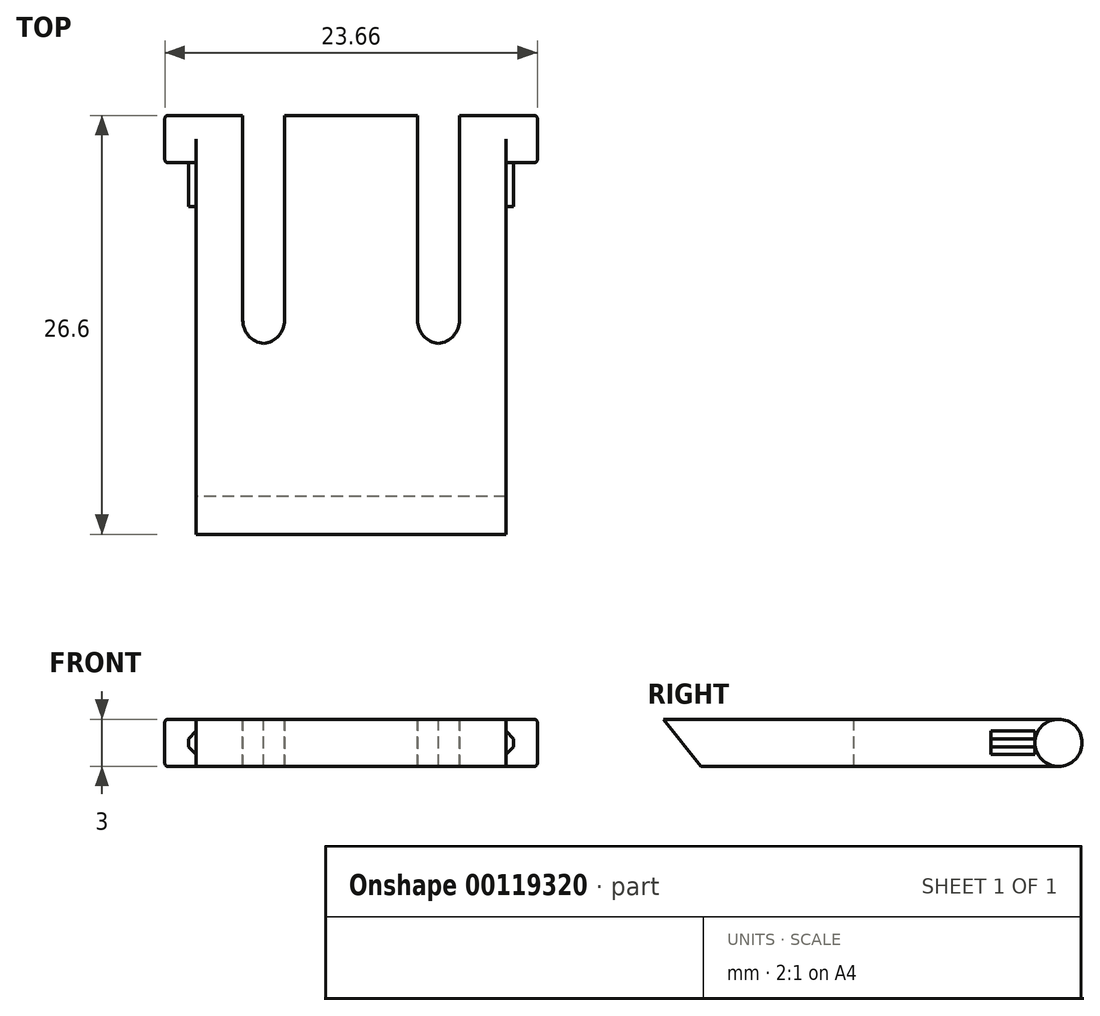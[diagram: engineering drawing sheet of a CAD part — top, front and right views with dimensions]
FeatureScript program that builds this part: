
annotation { "Feature Type Name" : "Feature", "Feature Type Description" : "" }
export const myFeature = defineFeature(function(context is Context, id is Id, definition is map)
    precondition{}
    {
        {
            var Q0;
            Q0=qCreatedBy(makeId("Top.planeOp"),FACE);
            var sketch = newSketch(context, id + "F0", { "sketchPlane" : qUnion([Q0])});
            skLineSegment(sketch, "E0.bottom", {"start": v(-29.8, 15.65) * mm, "end": v(-10.13, 15.65) * mm});
            skLineSegment(sketch, "E0.top", {"start": v(-29.8, -10.95) * mm, "end": v(-10.13, -10.95) * mm});
            skLineSegment(sketch, "E0.left", {"start": v(-29.8, 15.65) * mm, "end": v(-29.8, -10.95) * mm});
            skLineSegment(sketch, "E0.right", {"start": v(-10.13, 15.65) * mm, "end": v(-10.13, -10.95) * mm});
            skPoint(sketch, "E1", {"position": v(-13.08, 15.65) * mm});
            skPoint(sketch, "E2", {"position": v(-26.84, 15.65) * mm});
            skPoint(sketch, "E3", {"position": v(-24.18, 15.65) * mm});
            skPoint(sketch, "E4", {"position": v(-15.74, 15.65) * mm});
            skLineSegment(sketch, "E5.bottom", {"start": v(-26.84, 15.65) * mm, "end": v(-24.18, 15.65) * mm});
            skLineSegment(sketch, "E5.top", {"start": v(-26.84, 1.15) * mm, "end": v(-24.18, 1.15) * mm});
            skLineSegment(sketch, "E5.left", {"start": v(-26.84, 15.65) * mm, "end": v(-26.84, 1.15) * mm});
            skLineSegment(sketch, "E5.right", {"start": v(-24.18, 15.65) * mm, "end": v(-24.18, 1.15) * mm});
            skLineSegment(sketch, "E6.bottom", {"start": v(-13.08, 15.65) * mm, "end": v(-15.74, 15.65) * mm});
            skLineSegment(sketch, "E6.top", {"start": v(-13.08, 1.15) * mm, "end": v(-15.74, 1.15) * mm});
            skLineSegment(sketch, "E6.left", {"start": v(-13.08, 15.65) * mm, "end": v(-13.08, 1.15) * mm});
            skLineSegment(sketch, "E6.right", {"start": v(-15.74, 15.65) * mm, "end": v(-15.74, 1.15) * mm});
            skSolve(sketch);
        }
        {
            var Q0;
            Q0=makeQuery(id+"F0.imprint","IMPRINT",FACE,{"disambiguationData":[TD([[makeQuery(id+"F0.imprint","IMPRINT",EDGE,{"derivedFrom":sQuery(id+"F0.wireOp",EDGE,"E0.top")}),1.0]])]});
            extrude(context, id + "F1", {"entities" : qUnion([Q0]), "depth" : 3 * mm});
        }
        {
            var Q0;
            Q0=makeQuery(id+"F1.opExtrude","SWEPT_FACE",FACE,{"disambiguationData":[OSD([sQuery(id+"F0.wireOp",EDGE,"E0.right")])]});
            var sketch = newSketch(context, id + "F2", { "sketchPlane" : qUnion([Q0])});
            skPoint(sketch, "E7", {"position": v(14.15, 1.5) * mm});
            skPoint(sketch, "E7.positionSnap0", {"position": v(15.65, 1.5) * mm});
            skCircle(sketch, "E8", {"center": v(14.15, 1.5) * mm, "radius": 1.5 * mm});
            skPoint(sketch, "E9", {"position": v(12.65, 1.5) * mm});
            skPoint(sketch, "E10", {"position": v(12.65, 2.25) * mm});
            skLineSegment(sketch, "E11.bottom", {"start": v(12.65, 2.25) * mm, "end": v(9.85, 2.25) * mm});
            skLineSegment(sketch, "E11.top", {"start": v(12.65, 0.75) * mm, "end": v(9.85, 0.75) * mm});
            skLineSegment(sketch, "E11.left", {"start": v(12.65, 2.25) * mm, "end": v(12.65, 0.75) * mm});
            skLineSegment(sketch, "E11.right", {"start": v(9.85, 2.25) * mm, "end": v(9.85, 0.75) * mm});
            skSolve(sketch);
        }
        {
            var Q0;
            {var subQ0=sQuery(id+"F2.wireOp",EDGE,"E8");var subQ1=sQuery(id+"F0.wireOp",EDGE,"E0.right");var subQ2=makeQuery(id+"F2.imprint","INTERSECT",VERTEX,{"derivedFrom":[makeQuery(id+"F1.opExtrude","CAP_EDGE",EDGE,{"disambiguationData":[OSD([subQ1])],"isStart":false}),subQ0]});Q0=makeQuery(id+"F2.imprint","IMPRINT",FACE,{"disambiguationData":[TD([[makeQuery(id+"F2.imprint","IMPRINT",EDGE,{"disambiguationData":[TD([[subQ2,-1.0]])],"derivedFrom":subQ0}),1.0]])]});}
            extrude(context, id + "F3", {"entities" : qUnion([Q0]), "operationType" : NewBodyOperationType.ADD, "depth" : 2 * mm});
        }
        {
            var Q0;
            Q0=makeQuery(id+"F1.opExtrude","SWEPT_FACE",FACE,{"disambiguationData":[OSD([sQuery(id+"F0.wireOp",EDGE,"E0.left")])]});
            var sketch = newSketch(context, id + "F4", { "sketchPlane" : qUnion([Q0])});
            skPoint(sketch, "E12", {"position": v(-14.15, 1.5) * mm});
            skPoint(sketch, "E12.positionSnap0", {"position": v(-15.65, 1.5) * mm});
            skCircle(sketch, "E13", {"center": v(-14.15, 1.5) * mm, "radius": 1.5 * mm});
            skLineSegment(sketch, "E14.top", {"start": v(-12.65, 0.75) * mm, "end": v(-9.85, 0.75) * mm});
            skLineSegment(sketch, "E14.right", {"start": v(-9.85, 1.5) * mm, "end": v(-9.85, 0.75) * mm});
            skLineSegment(sketch, "E15.top", {"start": v(-12.65, 2.25) * mm, "end": v(-9.85, 2.25) * mm});
            skLineSegment(sketch, "E15.right", {"start": v(-9.85, 1.5) * mm, "end": v(-9.85, 2.25) * mm});
            skLineSegment(sketch, "E16", {"start": v(-12.65, 0.75) * mm, "end": v(-12.65, 2.25) * mm});
            skPoint(sketch, "E17", {"position": v(-4.7, 1.92) * mm});
            skPoint(sketch, "E18", {"position": v(8.55, 0) * mm});
            skLineSegment(sketch, "E19", {"start": v(8.55, 0) * mm, "end": v(10.95, 3) * mm});
            skSolve(sketch);
        }
        {
            var Q0;
            {var subQ0=sQuery(id+"F4.wireOp",EDGE,"E13");var subQ2=sQuery(id+"F0.wireOp",EDGE,"E0.left");var subQ3=makeQuery(id+"F4.imprint","INTERSECT",VERTEX,{"derivedFrom":[makeQuery(id+"F1.opExtrude","CAP_EDGE",EDGE,{"disambiguationData":[OSD([subQ2])],"isStart":false}),subQ0]});Q0=makeQuery(id+"F4.imprint","IMPRINT",FACE,{"disambiguationData":[TD([[makeQuery(id+"F4.imprint","IMPRINT",EDGE,{"disambiguationData":[TD([[subQ3,1.0]])],"derivedFrom":subQ0}),1.0]])]});}
            extrude(context, id + "F5", {"entities" : qUnion([Q0]), "operationType" : NewBodyOperationType.ADD, "depth" : 2 * mm});
        }
        {
            var Q0;
            {var subQ1=sQuery(id+"F4.wireOp",EDGE,"E14.top");Q0=makeQuery(id+"F4.imprint","IMPRINT",FACE,{"disambiguationData":[TD([[makeQuery(id+"F4.imprint","IMPRINT",EDGE,{"derivedFrom":subQ1}),1.0]])]});}
            extrude(context, id + "F6", {"entities" : qUnion([Q0]), "depth" : 0.5 * mm});
        }
        {
            var Q0;
            Q0=makeQuery(id+"F6.opExtrude","CAP_EDGE",EDGE,{"disambiguationData":[OSD([sQuery(id+"F4.wireOp",EDGE,"E14.top")])],"isStart":false});
            var Q1;
            Q1=makeQuery(id+"F6.opExtrude","CAP_EDGE",EDGE,{"disambiguationData":[OSD([sQuery(id+"F4.wireOp",EDGE,"E15.top")])],"isStart":false});
            chamfer(context, id + "F7", {"entities" : qUnion([Q0, Q1]), "width" : 0.5 * mm, "tangentPropagation" : true});
        }
        {
            var Q0;
            {var subQ3=sQuery(id+"F2.wireOp",EDGE,"E11.bottom");Q0=makeQuery(id+"F2.imprint","IMPRINT",FACE,{"disambiguationData":[TD([[makeQuery(id+"F2.imprint","IMPRINT",EDGE,{"derivedFrom":subQ3}),1.0]])]});}
            extrude(context, id + "F8", {"entities" : qUnion([Q0]), "depth" : 0.5 * mm});
        }
        {
            var Q0;
            Q0=makeQuery(id+"F8.opExtrude","CAP_EDGE",EDGE,{"disambiguationData":[OSD([sQuery(id+"F2.wireOp",EDGE,"E11.bottom")])],"isStart":false});
            var Q1;
            Q1=makeQuery(id+"F8.opExtrude","CAP_EDGE",EDGE,{"disambiguationData":[OSD([sQuery(id+"F2.wireOp",EDGE,"E11.top")])],"isStart":false});
            chamfer(context, id + "F9", {"entities" : qUnion([Q0, Q1]), "width" : 0.5 * mm, "tangentPropagation" : true});
        }
        {
            var Q0;
            {var subQ0=sQuery(id+"F4.wireOp",EDGE,"E19");Q0=makeQuery(id+"F4.imprint","IMPRINT",FACE,{"disambiguationData":[TD([[makeQuery(id+"F4.imprint","IMPRINT",EDGE,{"derivedFrom":subQ0}),-1.0]])]});}
            extrude(context, id + "F10", {"entities" : qUnion([Q0]), "operationType" : NewBodyOperationType.REMOVE, "endBound" : BoundingType.UP_TO_NEXT, "oppositeDirection" : true, "depth" : 25 * mm});
        }
        {
            var Q0;
            {var subQ0=sQuery(id+"F0.wireOp",EDGE,"E0.bottom");Q0=makeQuery(id+"F1.opExtrude","CAP_EDGE",EDGE,{"disambiguationData":[OSD([subQ0]),TDD([makeQuery(id+"F0.imprint","IMPRINT",EDGE,{"disambiguationData":[TD([[makeQuery(id+"F0.imprint","INTERSECT",VERTEX,{"derivedFrom":[subQ0,sQuery(id+"F0.wireOp",EDGE,"E5.bottom"),sQuery(id+"F0.wireOp",EDGE,"E5.right")]}),-1.0]])],"derivedFrom":subQ0})])],"isStart":false});}
            var Q1;
            {var subQ0=sQuery(id+"F0.wireOp",EDGE,"E0.bottom");Q1=makeQuery(id+"F1.opExtrude","CAP_EDGE",EDGE,{"disambiguationData":[OSD([subQ0]),TDD([makeQuery(id+"F0.imprint","IMPRINT",EDGE,{"disambiguationData":[TD([[makeQuery(id+"F0.imprint","INTERSECT",VERTEX,{"derivedFrom":[subQ0,sQuery(id+"F0.wireOp",EDGE,"E5.bottom"),sQuery(id+"F0.wireOp",EDGE,"E5.right")]}),-1.0]])],"derivedFrom":subQ0})])],"isStart":true});}
            fillet(context, id + "F11", {"entities" : qUnion([Q0, Q1]), "radius" : 1.5 * mm, "tangentPropagation" : true, "allowEdgeOverflow" : false});
        }
        {
            var Q0;
            {var subQ0=sQuery(id+"F0.wireOp",EDGE,"E0.bottom");Q0=makeQuery(id+"F1.opExtrude","CAP_EDGE",EDGE,{"disambiguationData":[OSD([subQ0]),TDD([makeQuery(id+"F0.imprint","IMPRINT",EDGE,{"disambiguationData":[TD([[makeQuery(id+"F0.imprint","INTERSECT",VERTEX,{"derivedFrom":[subQ0,sQuery(id+"F0.wireOp",EDGE,"E0.left")]}),-1.0]])],"derivedFrom":subQ0})])],"isStart":false});}
            var Q1;
            {var subQ0=sQuery(id+"F0.wireOp",EDGE,"E0.bottom");Q1=makeQuery(id+"F1.opExtrude","CAP_EDGE",EDGE,{"disambiguationData":[OSD([subQ0]),TDD([makeQuery(id+"F0.imprint","IMPRINT",EDGE,{"disambiguationData":[TD([[makeQuery(id+"F0.imprint","INTERSECT",VERTEX,{"derivedFrom":[subQ0,sQuery(id+"F0.wireOp",EDGE,"E0.left")]}),-1.0]])],"derivedFrom":subQ0})])],"isStart":true});}
            fillet(context, id + "F12", {"entities" : qUnion([Q0, Q1]), "radius" : 1.5 * mm, "tangentPropagation" : true, "allowEdgeOverflow" : false});
        }
        {
            var Q0;
            {var subQ0=sQuery(id+"F0.wireOp",EDGE,"E0.bottom");Q0=makeQuery(id+"F1.opExtrude","CAP_EDGE",EDGE,{"disambiguationData":[OSD([subQ0]),TDD([makeQuery(id+"F0.imprint","IMPRINT",EDGE,{"disambiguationData":[TD([[makeQuery(id+"F0.imprint","INTERSECT",VERTEX,{"derivedFrom":[subQ0,sQuery(id+"F0.wireOp",EDGE,"E0.right")]}),1.0]])],"derivedFrom":subQ0})])],"isStart":false});}
            var Q1;
            {var subQ0=sQuery(id+"F0.wireOp",EDGE,"E0.bottom");Q1=makeQuery(id+"F1.opExtrude","CAP_EDGE",EDGE,{"disambiguationData":[OSD([subQ0]),TDD([makeQuery(id+"F0.imprint","IMPRINT",EDGE,{"disambiguationData":[TD([[makeQuery(id+"F0.imprint","INTERSECT",VERTEX,{"derivedFrom":[subQ0,sQuery(id+"F0.wireOp",EDGE,"E0.right")]}),1.0]])],"derivedFrom":subQ0})])],"isStart":true});}
            fillet(context, id + "F13", {"entities" : qUnion([Q0, Q1]), "radius" : 1.5 * mm, "tangentPropagation" : true, "allowEdgeOverflow" : false});
        }
        {
            var Q0;
            Q0=makeQuery(id+"F3.opExtrude","CAP_EDGE",EDGE,{"disambiguationData":[OSD([sQuery(id+"F2.wireOp",EDGE,"E8")])],"isStart":false});
            fillet(context, id + "F14", {"entities" : qUnion([Q0]), "radius" : 0.2 * mm, "tangentPropagation" : true, "allowEdgeOverflow" : false});
        }
        {
            var Q0;
            Q0=makeQuery(id+"F5.opExtrude","CAP_FACE",FACE,{"disambiguationData":[OSD([sQuery(id+"F4.wireOp",EDGE,"E13")])],"isStart":false});
            fillet(context, id + "F15", {"entities" : qUnion([Q0]), "radius" : 0.2 * mm, "tangentPropagation" : true, "allowEdgeOverflow" : false});
        }
        {
            var Q0;
            Q0=makeQuery(id+"F1.opExtrude","SWEPT_EDGE",EDGE,{"disambiguationData":[OSD([sQuery(id+"F0.wireOp",EDGE,"E5.top"),sQuery(id+"F0.wireOp",EDGE,"E5.left")])]});
            var Q1;
            Q1=makeQuery(id+"F1.opExtrude","SWEPT_EDGE",EDGE,{"disambiguationData":[OSD([sQuery(id+"F0.wireOp",EDGE,"E5.top"),sQuery(id+"F0.wireOp",EDGE,"E5.right")])]});
            var Q2;
            Q2=makeQuery(id+"F1.opExtrude","SWEPT_EDGE",EDGE,{"disambiguationData":[OSD([sQuery(id+"F0.wireOp",EDGE,"E6.top"),sQuery(id+"F0.wireOp",EDGE,"E6.left")])]});
            var Q3;
            Q3=makeQuery(id+"F1.opExtrude","SWEPT_EDGE",EDGE,{"disambiguationData":[OSD([sQuery(id+"F0.wireOp",EDGE,"E6.top"),sQuery(id+"F0.wireOp",EDGE,"E6.right")])]});
            fillet(context, id + "F16", {"entities" : qUnion([Q0, Q1, Q2, Q3]), "radius" : 1.5 * mm, "tangentPropagation" : true, "allowEdgeOverflow" : false});
        }
    });
